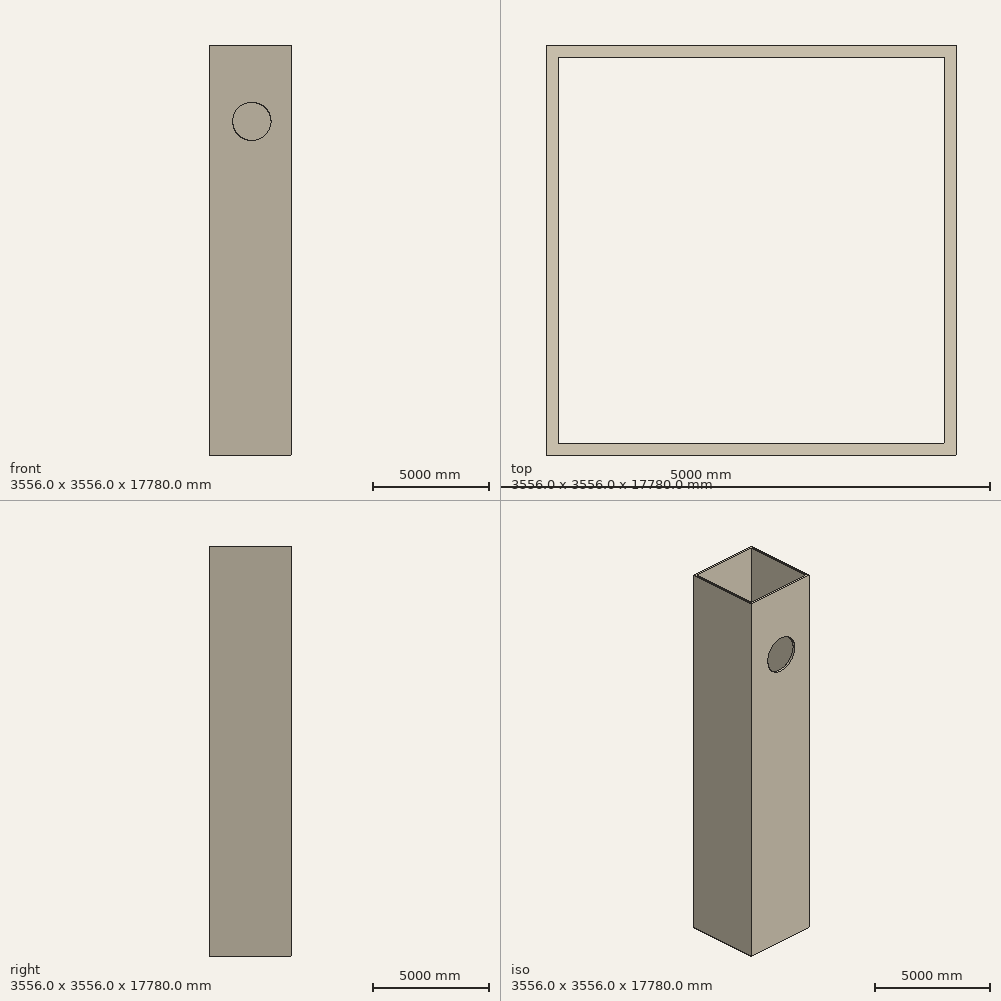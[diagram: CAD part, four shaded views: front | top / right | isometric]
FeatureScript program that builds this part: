
annotation { "Feature Type Name" : "Feature", "Feature Type Description" : "" }
export const myFeature = defineFeature(function(context is Context, id is Id, definition is map)
    precondition{}
    {
        {
            var Q0;
            Q0=qCreatedBy(makeId("Top.planeOp"),FACE);
            var sketch = newSketch(context, id + "F0", { "sketchPlane" : qUnion([Q0])});
            skLineSegment(sketch, "E0.bottom", {"start": v(0, 0) * mm, "end": v(3556, 0) * mm});
            skLineSegment(sketch, "E0.top", {"start": v(0, 3556) * mm, "end": v(3556, 3556) * mm});
            skLineSegment(sketch, "E0.left", {"start": v(0, 0) * mm, "end": v(0, 3556) * mm});
            skLineSegment(sketch, "E0.right", {"start": v(3556, 0) * mm, "end": v(3556, 3556) * mm});
            skLineSegment(sketch, "E1.bottom", {"start": v(3454.4, 3454.4) * mm, "end": v(101.6, 3454.4) * mm});
            skLineSegment(sketch, "E1.top", {"start": v(3454.4, 101.6) * mm, "end": v(101.6, 101.6) * mm});
            skLineSegment(sketch, "E1.left", {"start": v(3454.4, 3454.4) * mm, "end": v(3454.4, 101.6) * mm});
            skLineSegment(sketch, "E1.right", {"start": v(101.6, 3454.4) * mm, "end": v(101.6, 101.6) * mm});
            skSolve(sketch);
        }
        {
            var Q0;
            Q0=makeQuery(id+"F0.imprint","IMPRINT",FACE,{"disambiguationData":[TD([[makeQuery(id+"F0.imprint","IMPRINT",EDGE,{"derivedFrom":sQuery(id+"F0.wireOp",EDGE,"E0.bottom")}),1.0]])]});
            extrude(context, id + "F1", {"entities" : qUnion([Q0]), "depth" : 17780 * mm});
        }
        {
            var Q0;
            Q0=makeQuery(id+"F1.opExtrude","SWEPT_FACE",FACE,{"disambiguationData":[OSD([sQuery(id+"F0.wireOp",EDGE,"E0.bottom")])]});
            var sketch = newSketch(context, id + "F2", { "sketchPlane" : qUnion([Q0])});
            skCircle(sketch, "E2", {"center": v(1839.04, 14483.2) * mm, "radius": 831.4 * mm});
            skCircle(sketch, "E3", {"center": v(1509.8, 3605.76) * mm, "radius": 967.03 * mm});
            skSolve(sketch);
        }
        {
            var Q0;
            Q0=makeQuery(id+"F2.imprint","IMPRINT",FACE,{"disambiguationData":[TD([[makeQuery(id+"F2.imprint","IMPRINT",EDGE,{"derivedFrom":sQuery(id+"F2.wireOp",EDGE,"E2")}),1.0]])]});
            extrude(context, id + "F3", {"entities" : qUnion([Q0]), "operationType" : NewBodyOperationType.REMOVE, "oppositeDirection" : true, "depth" : 254 * mm});
        }
    });
